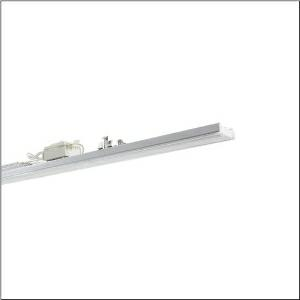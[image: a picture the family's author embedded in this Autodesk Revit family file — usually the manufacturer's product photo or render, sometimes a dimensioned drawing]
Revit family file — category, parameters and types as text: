
# Revit family: licross_r__21_recessed_ho_52te12dv4l2m3s_586b
name_source: partatom
category: Lighting Fixtures
units: mm (PartAtom-declared; Revit-internal decimal feet)

## family parameters
Cut with Voids When Loaded = No
Host = Face
Light Source = No
Part Type = Normal
Room Calculation Point = No
Round Connector Dimension = Use Diameter
Shared = No

## types (1)
- --- (1 x LED, 910 lm, 6.4 W, 4000K)
    Apparent Load = 6 VA
    CIE Flux Codes = 69 91 98 100 100
    Color Rendering = 80
    Color Temperature = 4000K
    Default Elevation = 1800 mm
    Description = Licross® 21 Recessed HO, luminaire insert, of sheet steel, galvanised, coil coated, white, length: 2.250mm, width: 66mm, height: 67mm, LED rated luminous flux: 22.710lm, light colour: 840, control gear: DALI 2 (for two DALI lines), with plug, 6-pole, with phase selection, for trunking rail, 14-core, mains connection: 220..240V, AC, 50/60Hz, rated input power: 129W, for trunking rail, 14-core, internal wiring halogen-free, for emergency light function, converter,control gear: single battery element, battery: LiFePO4, 9Ah, primary optical cover: cover, of PMMA, light emission: direct distribution, primary light characteristic: symmetric, protection rating (complete): IP54, insulation class (complete): insulation class I (protective earthing), certification: CE, UKCA, protection symbol: D if used in an environment with non-conductive dust loads with corresponding accessories, impact resistance: IK06, permissible ambient temperature for indoor applications: +5..+30°C, standard: EN 60598-2-22, LABS conformity tested according to VDMA 24364:2018-05, reducing of maximum allowable ambient temperature of 5°C with ceiling mounting, corresponds to IFS (International Featured Standards) requirements for safety and quality in the food industry, packaging unit: 1 piece
    Height = 58 mm
    Lamp = 1 x LED
    Lamp Light Flux = 910 lm
    Lamp Power = 6.4 W
    Lamp count = 1
    Length = 2250 mm
    Luminous efficacy = 142 lm/W
    Manufacturer = Siteco
    ModVariant = No
    Model = 52TE12DV4L2M3S
    Mounting Place = Ceiling
    Mounting Type = Pendant
    Number of Poles = 1
    OnlyDefault = Yes
    Power Factor = 1
    Product Name = Licross® 21 Recessed HO
    Product group = luminaire insert | ceiling pendant
    ProductGroupID = 902
    Protection Class = Protection class I
    Protection Degree = IP 54
    RLX_Detail_Level = 1
    RLX_Emergency_Light_Flux = 0 lm
    RLX_Emergency_Type = 0
    RLX_Emergency_Type_DB = No
    RlxData = <blob elided: 30081 chars, md5=66817f43>
    Socket = socket
    Standby Power = 0 W
    System Light Flux = 910 lm
    System Power = 6 W
    Type Comments = : emergency light operation: 3 h
    Type Image = l_1296930.jpg
    URL = http://relux.com
    VarID = @adj_130767
    Voltage = 0 V
    Weight = 0.00 kg
    Width = 66 mm

## geometry (parser evidence)
native form markers: Blend x4, Sweep x8
no freeform markers — native parametric forms only
